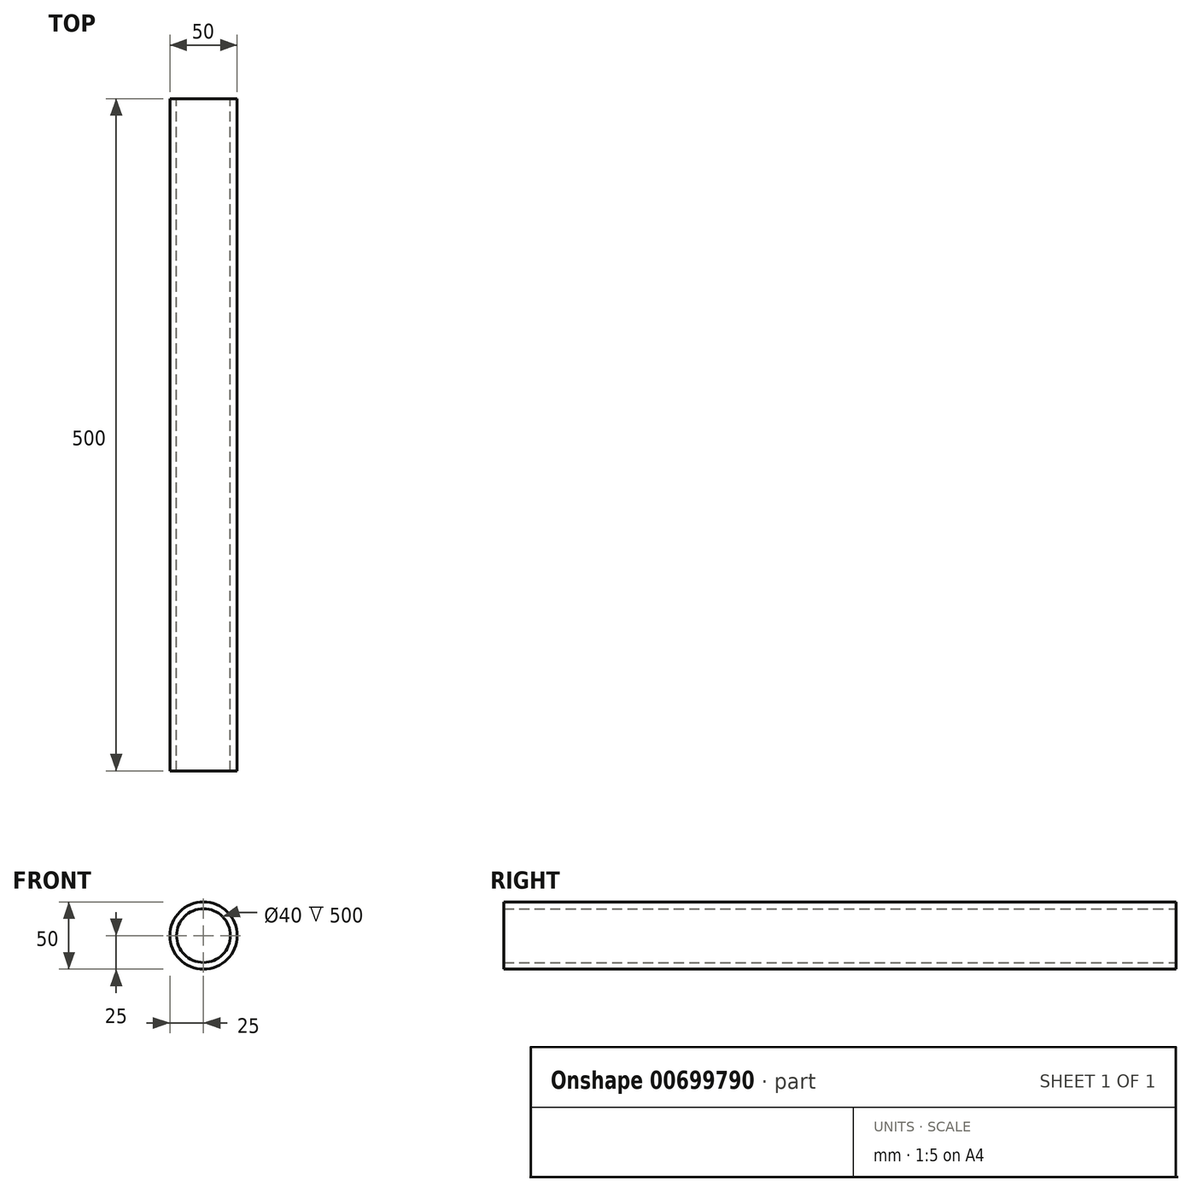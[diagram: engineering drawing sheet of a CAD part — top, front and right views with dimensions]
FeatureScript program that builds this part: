
annotation { "Feature Type Name" : "Feature", "Feature Type Description" : "" }
export const myFeature = defineFeature(function(context is Context, id is Id, definition is map)
    precondition{}
    {
        {
            var Q0;
            Q0=qCreatedBy(makeId("Front.planeOp"),FACE);
            var sketch = newSketch(context, id + "F0", { "sketchPlane" : qUnion([Q0])});
            skCircle(sketch, "E0", {"center": v(0, 0) * mm, "radius": 25 * mm});
            skSolve(sketch);
        }
        {
            var Q0;
            Q0=qSketchRegion(id+"F0",true);
            extrude(context, id + "F1", {"entities" : qUnion([Q0]), "depth" : 500 * mm, "offsetDistance" : 25 * mm});
        }
        {
            var Q0;
            Q0=qCreatedBy(makeId("Front.planeOp"),FACE);
            var sketch = newSketch(context, id + "F2", { "sketchPlane" : qUnion([Q0])});
            skCircle(sketch, "E1", {"center": v(0, 0) * mm, "radius": 20 * mm});
            skSolve(sketch);
        }
        {
            var Q0;
            Q0=makeQuery(id+"F2.imprint","IMPRINT",FACE,{"disambiguationData":[TD([[makeQuery(id+"F2.imprint","IMPRINT",EDGE,{"derivedFrom":sQuery(id+"F2.wireOp",EDGE,"E1")}),1.0]])]});
            extrude(context, id + "F3", {"entities" : qUnion([Q0]), "operationType" : NewBodyOperationType.REMOVE, "depth" : 500 * mm, "offsetDistance" : 25 * mm});
        }
    });
